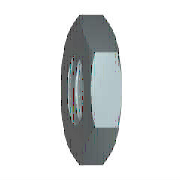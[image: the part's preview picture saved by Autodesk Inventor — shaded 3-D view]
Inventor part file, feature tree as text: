
AUTODESK INVENTOR PART (.ipt)
format: ipt  version: 2019 (Build 230136000, 136)  size: 172,544 bytes
history: native  units: mm (DEFAULTED — no unit token found)
features: sketch x3, chamfer x1, hole x1, other x1, plane x1
ambient origin geometry x7: Origin, YZ Plane, XZ Plane, X Axis, Y Axis, Z Axis, Center Point
bodies: Solid1 (feature_tree), Body (feature_tree)
feature tree (7):
  chamfer  "Chamfer1"  Angle=30.0deg  [1 undecoded]
  hole  "Thread"  [1 undecoded]
  other  "Work Axis1"
  plane  "Work Plane1"
  sketch  "Sketch1"  dims[d0=9.237604mm]
  sketch  "Sketch2"  dims[d1=2.7mm]
  sketch  "Sketch3"  dims[d2=0.0mm d3=30.0deg d4=30.0deg d5=6.9mm d6=6.9mm d7=90.0deg d25=4.134mm d26=6.0mm d27=4.0mm d28=2.0mm d29=14.3117mm d30=8.0mm d31=20.594885mm d8=0.433013mm d9=30.0deg d10=0.433013mm d11=30.0deg d13=0.0mm d14=0.0mm d39=0.0mm d40=0.433013mm d41=0.433013mm d42=0.0mm]
note: 2 required parameter values undecoded (feature->parameter linkage not recoverable at this tier; creation-order binding heuristic only, values carry confidence <= 0.55)
